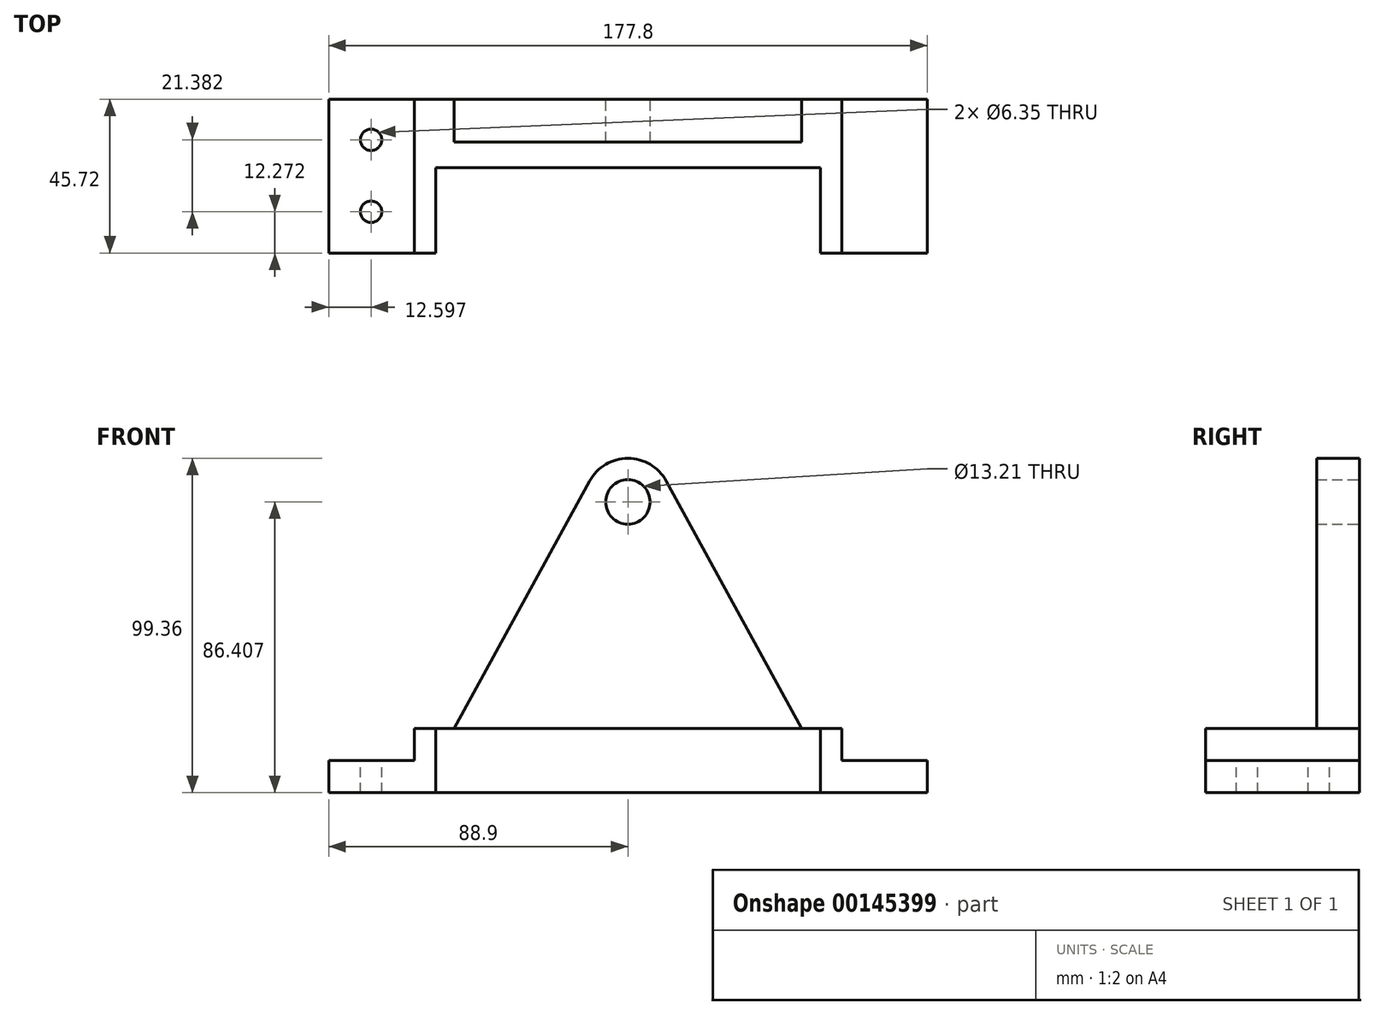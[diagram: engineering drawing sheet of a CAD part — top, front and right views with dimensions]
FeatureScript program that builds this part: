
annotation { "Feature Type Name" : "Feature", "Feature Type Description" : "" }
export const myFeature = defineFeature(function(context is Context, id is Id, definition is map)
    precondition{}
    {
        {
            var Q0;
            Q0=qCreatedBy(makeId("Front.planeOp"),FACE);
            var sketch = newSketch(context, id + "F0", { "sketchPlane" : qUnion([Q0])});
            skArc(sketch, "E0.0", {"start": v(31.68, -29.71) * mm, "mid": v(-0.48, 45.66) * mm, "end": v(-31.86, -30.04) * mm});
            skArc(sketch, "E1.0", {"start": v(41.11, -46.97) * mm, "mid": v(-0.48, 64.71) * mm, "end": v(-41.27, -47.26) * mm});
            skCircle(sketch, "E2", {"center": v(0, 1.2) * mm, "radius": 6.6 * mm});
            skArc(sketch, "E3.0", {"start": v(11.37, 7.42) * mm, "mid": v(0, 14.16) * mm, "end": v(-11.37, 7.42) * mm});
            skArc(sketch, "E4.0", {"start": v(34.85, -35.51) * mm, "mid": v(-0.48, 52.01) * mm, "end": v(-35.02, -35.83) * mm});
            skLineSegment(sketch, "E5.bottom", {"start": v(88.9, -85.2) * mm, "end": v(-88.9, -85.2) * mm});
            skLineSegment(sketch, "E5.top", {"start": v(63.5, -66.15) * mm, "end": v(-63.5, -66.15) * mm});
            skLineSegment(sketch, "E5.left", {"start": v(88.9, -85.2) * mm, "end": v(88.9, -75.68) * mm});
            skLineSegment(sketch, "E5.right", {"start": v(-88.9, -85.2) * mm, "end": v(-88.9, -75.68) * mm});
            skPoint(sketch, "E5.middle", {"position": v(0, -75.68) * mm});
            skLineSegment(sketch, "E6", {"start": v(-11.37, 7.42) * mm, "end": v(-51.6, -66.15) * mm});
            skLineSegment(sketch, "E7.MirrorCS", {"start": v(11.37, 7.42) * mm, "end": v(51.6, -66.15) * mm});
            skPoint(sketch, "E8.oppositeSnap0", {"position": v(-88.9, -75.68) * mm});
            skLineSegment(sketch, "E8.top", {"start": v(-88.9, -75.68) * mm, "end": v(-63.5, -75.68) * mm});
            skLineSegment(sketch, "E8.right", {"start": v(-63.5, -66.15) * mm, "end": v(-63.5, -75.68) * mm});
            skLineSegment(sketch, "E9.MirrorCS", {"start": v(88.9, -75.68) * mm, "end": v(63.5, -75.68) * mm});
            skLineSegment(sketch, "E10.MirrorCS", {"start": v(63.5, -66.15) * mm, "end": v(63.5, -75.68) * mm});
            skPoint(sketch, "E11.orphan", {"position": v(-88.9, -66.15) * mm});
            skPoint(sketch, "E12.orphan", {"position": v(88.9, -66.15) * mm});
            skSolve(sketch);
        }
        {
            var Q0;
            Q0=makeQuery(id+"F0.imprint","IMPRINT",FACE,{"disambiguationData":[TD([[makeQuery(id+"F0.imprint","IMPRINT",EDGE,{"derivedFrom":sQuery(id+"F0.wireOp",EDGE,"E2")}),-1.0]])]});
            extrude(context, id + "F1", {"entities" : qUnion([Q0]), "depth" : 12.7 * mm});
        }
        {
            var Q0;
            Q0=makeQuery(id+"F0.imprint","IMPRINT",FACE,{"disambiguationData":[TD([[makeQuery(id+"F0.imprint","IMPRINT",EDGE,{"derivedFrom":sQuery(id+"F0.wireOp",EDGE,"E5.bottom")}),-1.0]])]});
            extrude(context, id + "F2", {"entities" : qUnion([Q0]), "operationType" : NewBodyOperationType.ADD, "depth" : 45.72 * mm});
        }
        {
            var Q0;
            Q0=makeQuery(id+"F2.opExtrude","SWEPT_FACE",FACE,{"disambiguationData":[OSD([sQuery(id+"F0.wireOp",EDGE,"E8.top")])]});
            var sketch = newSketch(context, id + "F3", { "sketchPlane" : qUnion([Q0])});
            skCircle(sketch, "E13", {"center": v(-76.3, -12.07) * mm, "radius": 3.18 * mm});
            skCircle(sketch, "E14", {"center": v(-76.3, -33.45) * mm, "radius": 3.18 * mm});
            skCircle(sketch, "E15.MirrorC", {"center": v(76.3, -12.07) * mm, "radius": 3.18 * mm});
            skCircle(sketch, "E16.MirrorC", {"center": v(76.3, -33.45) * mm, "radius": 3.18 * mm});
            skSolve(sketch);
        }
        {
            var Q0;
            Q0=makeQuery(id+"F3.imprint","IMPRINT",FACE,{"disambiguationData":[TD([[makeQuery(id+"F3.imprint","IMPRINT",EDGE,{"derivedFrom":sQuery(id+"F3.wireOp",EDGE,"E13")}),1.0]])]});
            var Q1;
            Q1=makeQuery(id+"F3.imprint","IMPRINT",FACE,{"disambiguationData":[TD([[makeQuery(id+"F3.imprint","IMPRINT",EDGE,{"derivedFrom":sQuery(id+"F3.wireOp",EDGE,"E14")}),1.0]])]});
            var Q2;
            Q2=makeQuery(id+"F3.imprint","IMPRINT",FACE,{"disambiguationData":[TD([[makeQuery(id+"F3.imprint","IMPRINT",EDGE,{"derivedFrom":sQuery(id+"F3.wireOp",EDGE,"E15.MirrorC")}),-1.0]])]});
            var Q3;
            Q3=makeQuery(id+"F3.imprint","IMPRINT",FACE,{"disambiguationData":[TD([[makeQuery(id+"F3.imprint","IMPRINT",EDGE,{"derivedFrom":sQuery(id+"F3.wireOp",EDGE,"E16.MirrorC")}),-1.0]])]});
            var Q4;
            Q4=sQuery(id+"F3.wireOp",EDGE,"E13");
            var Q5;
            Q5=sQuery(id+"F3.wireOp",EDGE,"E14");
            var Q6;
            Q6=sQuery(id+"F3.wireOp",EDGE,"E16.MirrorC");
            var Q7;
            Q7=sQuery(id+"F3.wireOp",EDGE,"E15.MirrorC");
            extrude(context, id + "F4", {"entities" : qUnion([Q0, Q1, Q2, Q3]), "operationType" : NewBodyOperationType.REMOVE, "surfaceEntities" : qUnion([Q4, Q5, Q6, Q7]), "endBound" : BoundingType.THROUGH_ALL, "oppositeDirection" : true, "depth" : 25.4 * mm});
        }
        {
            var Q0;
            Q0=makeQuery(id+"F2.opExtrude","SWEPT_FACE",FACE,{"disambiguationData":[OSD([sQuery(id+"F0.wireOp",EDGE,"E5.bottom")])]});
            var sketch = newSketch(context, id + "F5", { "sketchPlane" : qUnion([Q0])});
            skLineSegment(sketch, "E17.bottom", {"start": v(57.15, 20.32) * mm, "end": v(-57.15, 20.32) * mm});
            skLineSegment(sketch, "E17.left", {"start": v(57.15, 20.32) * mm, "end": v(57.15, 45.72) * mm});
            skLineSegment(sketch, "E17.right", {"start": v(-57.15, 20.32) * mm, "end": v(-57.15, 45.72) * mm});
            skPoint(sketch, "E17.middle", {"position": v(0, 45.72) * mm});
            skLineSegment(sketch, "E18", {"start": v(-57.15, 45.72) * mm, "end": v(57.15, 45.72) * mm});
            skPoint(sketch, "E19.orphan", {"position": v(57.15, 71.12) * mm});
            skPoint(sketch, "E20.orphan", {"position": v(-57.15, 71.12) * mm});
            skSolve(sketch);
        }
        {
            var Q0;
            Q0=makeQuery(id+"F5.imprint","IMPRINT",FACE,{"disambiguationData":[TD([[makeQuery(id+"F5.imprint","IMPRINT",EDGE,{"derivedFrom":sQuery(id+"F5.wireOp",EDGE,"E17.bottom")}),-1.0]])]});
            extrude(context, id + "F6", {"entities" : qUnion([Q0]), "operationType" : NewBodyOperationType.REMOVE, "endBound" : BoundingType.THROUGH_ALL, "oppositeDirection" : true, "depth" : 25.4 * mm});
        }
    });
